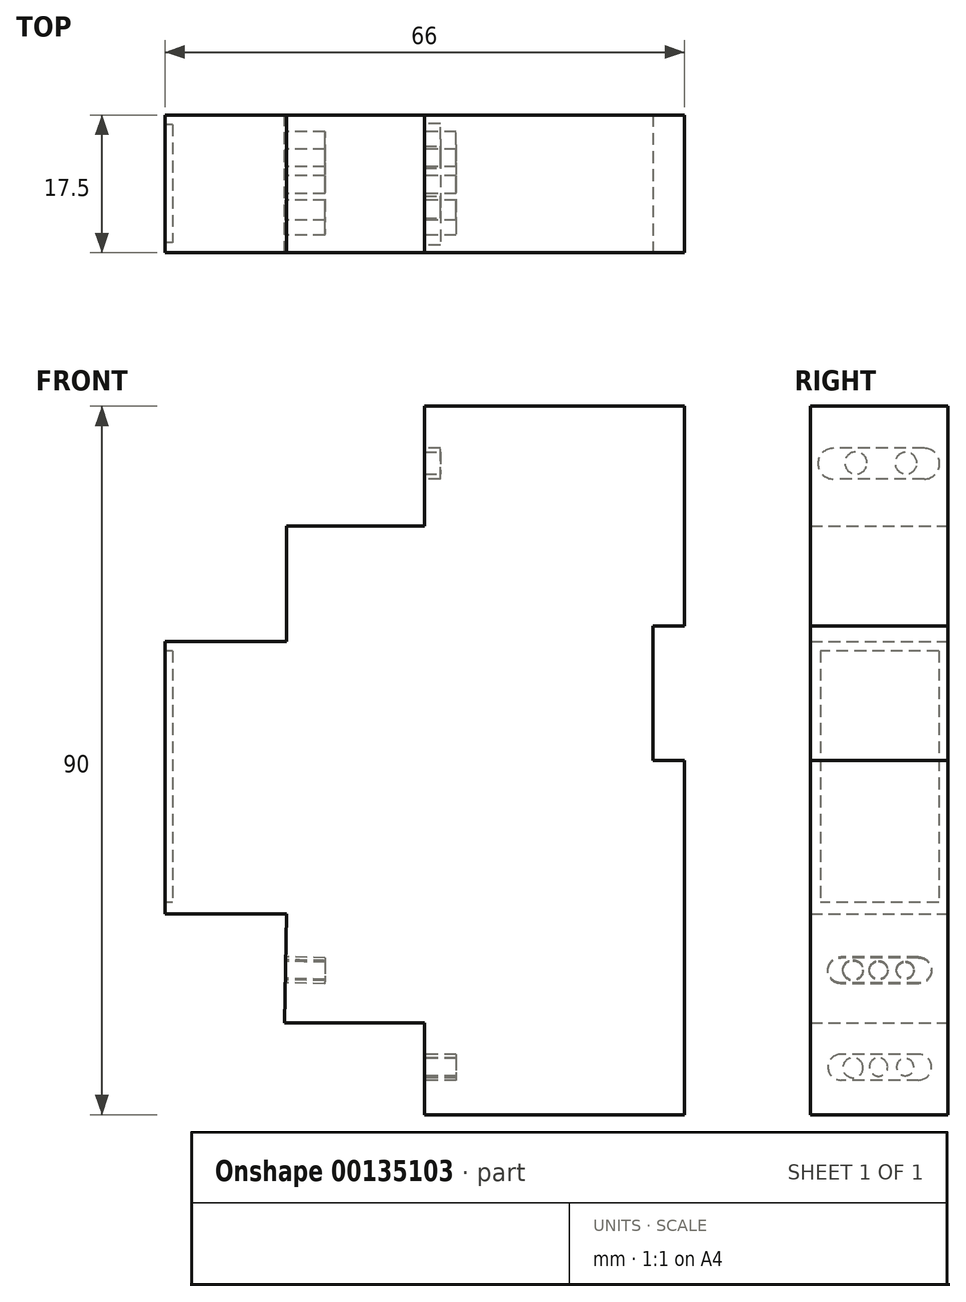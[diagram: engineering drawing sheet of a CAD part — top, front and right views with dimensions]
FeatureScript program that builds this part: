
annotation { "Feature Type Name" : "Feature", "Feature Type Description" : "" }
export const myFeature = defineFeature(function(context is Context, id is Id, definition is map)
    precondition{}
    {
        {
            var Q0;
            Q0=qCreatedBy(makeId("Front.planeOp"),FACE);
            var sketch = newSketch(context, id + "F0", { "sketchPlane" : qUnion([Q0])});
            skLineSegment(sketch, "E0.bottom", {"start": v(-62.04, 133.55) * mm, "end": v(-29.04, 133.55) * mm});
            skLineSegment(sketch, "E0.top", {"start": v(-62.04, 43.55) * mm, "end": v(-29.04, 43.55) * mm});
            skLineSegment(sketch, "E0.left", {"start": v(-95.04, 103.68) * mm, "end": v(-95.04, 69.08) * mm});
            skLineSegment(sketch, "E0.right", {"start": v(-29.04, 133.55) * mm, "end": v(-29.04, 43.55) * mm});
            skLineSegment(sketch, "E1", {"start": v(-62.04, 133.55) * mm, "end": v(-62.04, 118.36) * mm});
            skLineSegment(sketch, "E2", {"start": v(-62.04, 118.36) * mm, "end": v(-79.55, 118.36) * mm});
            skLineSegment(sketch, "E3", {"start": v(-79.55, 118.36) * mm, "end": v(-79.55, 103.68) * mm});
            skLineSegment(sketch, "E4", {"start": v(-79.55, 103.68) * mm, "end": v(-95.04, 103.68) * mm});
            skLineSegment(sketch, "E5", {"start": v(-95.04, 69.08) * mm, "end": v(-79.55, 69.08) * mm});
            skLineSegment(sketch, "E6", {"start": v(-79.55, 69.08) * mm, "end": v(-79.83, 55.24) * mm});
            skLineSegment(sketch, "E7", {"start": v(-79.83, 55.24) * mm, "end": v(-62.04, 55.24) * mm});
            skLineSegment(sketch, "E8", {"start": v(-62.04, 55.24) * mm, "end": v(-62.04, 43.55) * mm});
            skPoint(sketch, "E9.orphan", {"position": v(-95.04, 133.55) * mm});
            skPoint(sketch, "E10.orphan", {"position": v(-95.04, 43.55) * mm});
            skLineSegment(sketch, "E11", {"start": v(-29.04, 105.62) * mm, "end": v(-34.98, 105.62) * mm});
            skLineSegment(sketch, "E12", {"start": v(-34.98, 105.62) * mm, "end": v(-34.98, 66.59) * mm});
            skLineSegment(sketch, "E13", {"start": v(-34.98, 66.59) * mm, "end": v(-29.04, 66.59) * mm});
            skSolve(sketch);
        }
        {
            var Q0;
            {var subQ0=sQuery(id+"F0.wireOp",EDGE,"E0.bottom");Q0=makeQuery(id+"F0.imprint","IMPRINT",FACE,{"disambiguationData":[TD([[makeQuery(id+"F0.imprint","IMPRINT",EDGE,{"derivedFrom":subQ0}),-1.0]])]});}
            extrude(context, id + "F1", {"entities" : qUnion([Q0]), "depth" : 17.5 * mm});
        }
        {
            var Q0;
            Q0=makeQuery(id+"F1.opExtrude","SWEPT_FACE",FACE,{"disambiguationData":[OSD([sQuery(id+"F0.wireOp",EDGE,"E1")])]});
            var sketch = newSketch(context, id + "F2", { "sketchPlane" : qUnion([Q0])});
            skLineSegment(sketch, "E14.bottom", {"start": v(3.04, 128.2) * mm, "end": v(14.59, 128.2) * mm});
            skLineSegment(sketch, "E14.top", {"start": v(3.04, 124.3) * mm, "end": v(14.59, 124.3) * mm});
            skArc(sketch, "E15", {"start": v(14.59, 124.3) * mm, "mid": v(16.54, 126.26) * mm, "end": v(14.59, 128.2) * mm});
            skArc(sketch, "E16", {"start": v(3.04, 128.2) * mm, "mid": v(1.09, 126.26) * mm, "end": v(3.04, 124.3) * mm});
            skSolve(sketch);
        }
        {
            var Q0;
            Q0=makeQuery(id+"F2.imprint","IMPRINT",FACE,{"disambiguationData":[TD([[makeQuery(id+"F2.imprint","IMPRINT",EDGE,{"derivedFrom":sQuery(id+"F2.wireOp",EDGE,"E14.bottom")}),-1.0]])]});
            extrude(context, id + "F3", {"entities" : qUnion([Q0]), "operationType" : NewBodyOperationType.REMOVE, "oppositeDirection" : true, "depth" : 2 * mm});
        }
        {
            var Q0;
            Q0=makeQuery(id+"F3.boolean.opBoolean","COPY",FACE,{"derivedFrom":makeQuery(id+"F3.opExtrude","CAP_FACE",FACE,{"disambiguationData":[OSD([sQuery(id+"F2.wireOp",EDGE,"E14.bottom"),sQuery(id+"F2.wireOp",EDGE,"E14.top"),sQuery(id+"F2.wireOp",EDGE,"E15"),sQuery(id+"F2.wireOp",EDGE,"E16")])],"isStart":false})});
            var sketch = newSketch(context, id + "F4", { "sketchPlane" : qUnion([Q0])});
            skCircle(sketch, "E17", {"center": v(5.35, 126.32) * mm, "radius": 1.38 * mm});
            skCircle(sketch, "E18", {"center": v(11.71, 126.34) * mm, "radius": 1.41 * mm});
            skSolve(sketch);
        }
        {
            var Q0;
            Q0=makeQuery(id+"F4.imprint","IMPRINT",FACE,{"disambiguationData":[TD([[makeQuery(id+"F4.imprint","IMPRINT",EDGE,{"derivedFrom":sQuery(id+"F4.wireOp",EDGE,"E17")}),1.0]])]});
            var Q1;
            Q1=makeQuery(id+"F4.imprint","IMPRINT",FACE,{"disambiguationData":[TD([[makeQuery(id+"F4.imprint","IMPRINT",EDGE,{"derivedFrom":sQuery(id+"F4.wireOp",EDGE,"E18")}),1.0]])]});
            extrude(context, id + "F5", {"entities" : qUnion([Q0, Q1]), "operationType" : NewBodyOperationType.ADD, "depth" : 2 * mm});
        }
        {
            var Q0;
            Q0=makeQuery(id+"F1.opExtrude","SWEPT_FACE",FACE,{"disambiguationData":[OSD([sQuery(id+"F0.wireOp",EDGE,"E8")])]});
            var sketch = newSketch(context, id + "F6", { "sketchPlane" : qUnion([Q0])});
            skLineSegment(sketch, "E19.bottom", {"start": v(3.76, 51.23) * mm, "end": v(13.62, 51.23) * mm});
            skLineSegment(sketch, "E19.top", {"start": v(3.76, 47.94) * mm, "end": v(13.62, 47.94) * mm});
            skArc(sketch, "E20", {"start": v(3.76, 51.23) * mm, "mid": v(2.12, 49.58) * mm, "end": v(3.76, 47.94) * mm});
            skArc(sketch, "E21", {"start": v(13.62, 47.94) * mm, "mid": v(15.27, 49.58) * mm, "end": v(13.62, 51.23) * mm});
            skCircle(sketch, "E22", {"center": v(5.45, 49.58) * mm, "radius": 1.1 * mm});
            skPoint(sketch, "E22.centerSnap0", {"position": v(2.12, 49.58) * mm});
            skCircle(sketch, "E23", {"center": v(12.09, 49.5) * mm, "radius": 1.28 * mm});
            skCircle(sketch, "E24", {"center": v(8.84, 49.6) * mm, "radius": 1.16 * mm});
            skSolve(sketch);
        }
        {
            var Q0;
            Q0=makeQuery(id+"F6.imprint","IMPRINT",FACE,{"disambiguationData":[TD([[makeQuery(id+"F6.imprint","IMPRINT",EDGE,{"derivedFrom":sQuery(id+"F6.wireOp",EDGE,"E19.bottom")}),-1.0]])]});
            extrude(context, id + "F7", {"entities" : qUnion([Q0]), "operationType" : NewBodyOperationType.REMOVE, "oppositeDirection" : true, "depth" : 4 * mm});
        }
        {
            var Q0;
            Q0=makeQuery(id+"F1.opExtrude","CAP_FACE",FACE,{"disambiguationData":[OSD([sQuery(id+"F0.wireOp",EDGE,"E0.bottom"),sQuery(id+"F0.wireOp",EDGE,"E0.top"),sQuery(id+"F0.wireOp",EDGE,"E0.right"),sQuery(id+"F0.wireOp",EDGE,"E1"),sQuery(id+"F0.wireOp",EDGE,"E2"),sQuery(id+"F0.wireOp",EDGE,"E3"),sQuery(id+"F0.wireOp",EDGE,"E4"),sQuery(id+"F0.wireOp",EDGE,"E0.left"),sQuery(id+"F0.wireOp",EDGE,"E5"),sQuery(id+"F0.wireOp",EDGE,"E6"),sQuery(id+"F0.wireOp",EDGE,"E7"),sQuery(id+"F0.wireOp",EDGE,"E8"),sQuery(id+"F0.wireOp",EDGE,"E11"),sQuery(id+"F0.wireOp",EDGE,"E12"),sQuery(id+"F0.wireOp",EDGE,"E13")])],"isStart":false});
            var sketch = newSketch(context, id + "F8", { "sketchPlane" : qUnion([Q0])});
            skLineSegment(sketch, "E25", {"start": v(-29.04, 133.55) * mm, "end": v(-29.04, 43.55) * mm});
            skLineSegment(sketch, "E26.bottom", {"start": v(-29.04, 88.55) * mm, "end": v(-33.04, 88.55) * mm});
            skLineSegment(sketch, "E26.top", {"start": v(-29.04, 105.62) * mm, "end": v(-33.04, 105.62) * mm});
            skLineSegment(sketch, "E26.left", {"start": v(-29.04, 88.55) * mm, "end": v(-29.04, 105.62) * mm});
            skLineSegment(sketch, "E26.right", {"start": v(-33.04, 88.55) * mm, "end": v(-33.04, 105.62) * mm});
            skLineSegment(sketch, "E27.bottom", {"start": v(-33.04, 88.55) * mm, "end": v(-29.04, 88.55) * mm});
            skLineSegment(sketch, "E27.top", {"start": v(-33.04, 71.05) * mm, "end": v(-29.04, 71.05) * mm});
            skLineSegment(sketch, "E27.left", {"start": v(-33.04, 88.55) * mm, "end": v(-33.04, 71.05) * mm});
            skLineSegment(sketch, "E27.right", {"start": v(-29.04, 88.55) * mm, "end": v(-29.04, 71.05) * mm});
            skSolve(sketch);
        }
        {
            var Q0;
            Q0=makeQuery(id+"F1.opExtrude","SWEPT_FACE",FACE,{"disambiguationData":[OSD([sQuery(id+"F0.wireOp",EDGE,"E11")])]});
            extrude(context, id + "F9", {"entities" : qUnion([Q0]), "operationType" : NewBodyOperationType.ADD, "depth" : 42.87 * mm});
        }
        {
            var Q0;
            Q0=makeQuery(id+"F8.imprint","IMPRINT",FACE,{"disambiguationData":[TD([[makeQuery(id+"F8.imprint","IMPRINT",EDGE,{"derivedFrom":sQuery(id+"F8.wireOp",EDGE,"E26.top")}),1.0]])]});
            var Q1;
            Q1=makeQuery(id+"F8.imprint","IMPRINT",FACE,{"disambiguationData":[TD([[makeQuery(id+"F8.imprint","IMPRINT",EDGE,{"derivedFrom":sQuery(id+"F8.wireOp",EDGE,"E27.bottom")}),-1.0]])]});
            extrude(context, id + "F10", {"entities" : qUnion([Q0, Q1]), "operationType" : NewBodyOperationType.REMOVE, "oppositeDirection" : true, "depth" : 25 * mm});
        }
        {
            var Q0;
            Q0=makeQuery(id+"F1.opExtrude","SWEPT_FACE",FACE,{"disambiguationData":[OSD([sQuery(id+"F0.wireOp",EDGE,"E6")])]});
            var sketch = newSketch(context, id + "F11", { "sketchPlane" : qUnion([Q0])});
            skLineSegment(sketch, "E28.bottom", {"start": v(3.76, 61.98) * mm, "end": v(13.62, 61.98) * mm});
            skLineSegment(sketch, "E28.top", {"start": v(3.76, 58.69) * mm, "end": v(13.62, 58.69) * mm});
            skArc(sketch, "E29", {"start": v(3.76, 61.98) * mm, "mid": v(2.12, 60.33) * mm, "end": v(3.76, 58.69) * mm});
            skArc(sketch, "E30", {"start": v(13.62, 58.69) * mm, "mid": v(15.27, 60.33) * mm, "end": v(13.62, 61.98) * mm});
            skCircle(sketch, "E31", {"center": v(5.45, 60.33) * mm, "radius": 1.1 * mm});
            skPoint(sketch, "E31.centerSnap0", {"position": v(2.12, 60.33) * mm});
            skCircle(sketch, "E32", {"center": v(12.09, 60.33) * mm, "radius": 1.28 * mm});
            skCircle(sketch, "E33", {"center": v(8.84, 60.33) * mm, "radius": 1.16 * mm});
            skEllipse(sketch, "E34.1", {"center": v(8.84, 48.35) * mm, "majorRadius": 1.16 * mm, "minorRadius": 1.16 * mm, "majorAxis": v(-1, 0)});
            skEllipse(sketch, "E35.0", {"center": v(5.45, 48.33) * mm, "majorRadius": 1.1 * mm, "minorRadius": 1.1 * mm, "majorAxis": v(-1, 0)});
            skEllipse(sketch, "E36.0.0", {"center": v(12.09, 48.26) * mm, "majorRadius": 1.28 * mm, "minorRadius": 1.28 * mm, "majorAxis": v(-1, 0)});
            skEllipticalArc(sketch, "E37.0", {});
            const initialGuessF11  = {"E37.0": [0.003762326668947935, 0.0483326911488126, -1, 0, 0.0016468185931444168, 0.001646489330150957, 4.71238898038469, 1.5707963267948966]};
            skSetInitialGuess(sketch, initialGuessF11);
            skSolve(sketch);
        }
        {
            var Q0;
            Q0=makeQuery(id+"F11.imprint","IMPRINT",FACE,{"disambiguationData":[TD([[makeQuery(id+"F11.imprint","IMPRINT",EDGE,{"derivedFrom":sQuery(id+"F11.wireOp",EDGE,"E28.bottom")}),-1.0]])]});
            extrude(context, id + "F12", {"entities" : qUnion([Q0]), "operationType" : NewBodyOperationType.REMOVE, "oppositeDirection" : true, "depth" : 5 * mm});
        }
        {
            var Q0;
            Q0=makeQuery(id+"F1.opExtrude","SWEPT_FACE",FACE,{"disambiguationData":[OSD([sQuery(id+"F0.wireOp",EDGE,"E0.left")])]});
            var sketch = newSketch(context, id + "F13", { "sketchPlane" : qUnion([Q0])});
            skLineSegment(sketch, "E38.bottom", {"start": v(1.2, 102.48) * mm, "end": v(16.2, 102.48) * mm});
            skLineSegment(sketch, "E38.top", {"start": v(1.2, 70.48) * mm, "end": v(16.2, 70.48) * mm});
            skLineSegment(sketch, "E38.left", {"start": v(1.2, 102.48) * mm, "end": v(1.2, 70.48) * mm});
            skLineSegment(sketch, "E38.right", {"start": v(16.2, 102.48) * mm, "end": v(16.2, 70.48) * mm});
            skSolve(sketch);
        }
        {
            var Q0;
            Q0=makeQuery(id+"F13.imprint","IMPRINT",FACE,{"disambiguationData":[TD([[makeQuery(id+"F13.imprint","IMPRINT",EDGE,{"derivedFrom":sQuery(id+"F13.wireOp",EDGE,"E38.bottom")}),-1.0]])]});
            extrude(context, id + "F14", {"entities" : qUnion([Q0]), "operationType" : NewBodyOperationType.REMOVE, "oppositeDirection" : true, "depth" : 1 * mm});
        }
    });
